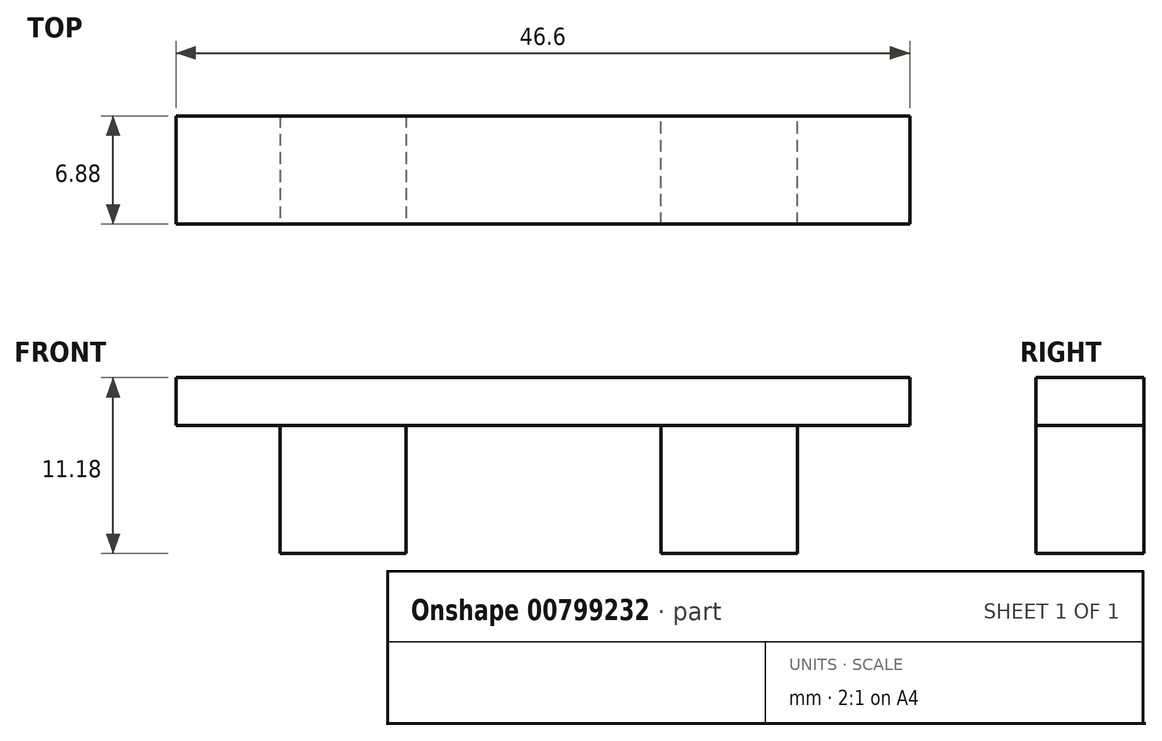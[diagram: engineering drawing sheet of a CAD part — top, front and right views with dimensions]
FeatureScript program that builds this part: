
annotation { "Feature Type Name" : "Feature", "Feature Type Description" : "" }
export const myFeature = defineFeature(function(context is Context, id is Id, definition is map)
    precondition{}
    {
        {
            var Q0;
            Q0=qCreatedBy(makeId("Top.planeOp"),FACE);
            var sketch = newSketch(context, id + "F0", { "sketchPlane" : qUnion([Q0])});
            skLineSegment(sketch, "E0.bottom", {"start": v(0, 0) * mm, "end": v(8.01, 0) * mm});
            skLineSegment(sketch, "E0.top", {"start": v(0, -6.88) * mm, "end": v(8.01, -6.88) * mm});
            skLineSegment(sketch, "E0.left", {"start": v(0, 0) * mm, "end": v(0, -6.88) * mm});
            skLineSegment(sketch, "E0.right", {"start": v(8.01, 0) * mm, "end": v(8.01, -6.88) * mm});
            skLineSegment(sketch, "E1.bottom", {"start": v(24.2, -6.88) * mm, "end": v(32.86, -6.88) * mm});
            skLineSegment(sketch, "E1.top", {"start": v(24.2, 0) * mm, "end": v(32.86, 0) * mm});
            skLineSegment(sketch, "E1.left", {"start": v(24.2, -6.88) * mm, "end": v(24.2, 0) * mm});
            skLineSegment(sketch, "E1.right", {"start": v(32.86, -6.88) * mm, "end": v(32.86, 0) * mm});
            skSolve(sketch);
        }
        {
            var Q0;
            Q0=makeQuery(id+"F0.imprint","IMPRINT",FACE,{"disambiguationData":[TD([[makeQuery(id+"F0.imprint","IMPRINT",EDGE,{"derivedFrom":sQuery(id+"F0.wireOp",EDGE,"E0.bottom")}),-1.0]])]});
            var Q1;
            Q1=makeQuery(id+"F0.imprint","IMPRINT",FACE,{"disambiguationData":[TD([[makeQuery(id+"F0.imprint","IMPRINT",EDGE,{"derivedFrom":sQuery(id+"F0.wireOp",EDGE,"E1.bottom")}),1.0]])]});
            extrude(context, id + "F1", {"entities" : qUnion([Q0, Q1]), "depth" : 8.13 * mm, "offsetDistance" : 25.4 * mm});
        }
        {
            var Q0;
            Q0=makeQuery(id+"F1.opExtrude","CAP_FACE",FACE,{"disambiguationData":[OSD([sQuery(id+"F0.wireOp",EDGE,"E0.bottom"),sQuery(id+"F0.wireOp",EDGE,"E0.top"),sQuery(id+"F0.wireOp",EDGE,"E0.left"),sQuery(id+"F0.wireOp",EDGE,"E0.right")])],"isStart":false});
            var sketch = newSketch(context, id + "F2", { "sketchPlane" : qUnion([Q0])});
            skLineSegment(sketch, "E2.bottom", {"start": v(-6.6, 0) * mm, "end": v(40, 0) * mm});
            skLineSegment(sketch, "E2.top", {"start": v(-6.6, -6.88) * mm, "end": v(40, -6.88) * mm});
            skLineSegment(sketch, "E2.left", {"start": v(-6.6, 0) * mm, "end": v(-6.6, -6.88) * mm});
            skLineSegment(sketch, "E2.right", {"start": v(40, 0) * mm, "end": v(40, -6.88) * mm});
            skSolve(sketch);
        }
        {
            var Q0;
            {var subQ2=sQuery(id+"F2.wireOp",EDGE,"E2.left");Q0=makeQuery(id+"F2.imprint","IMPRINT",FACE,{"disambiguationData":[TD([[makeQuery(id+"F2.imprint","IMPRINT",EDGE,{"derivedFrom":subQ2}),1.0]])]});}
            var Q1;
            {var subQ2=sQuery(id+"F2.wireOp",EDGE,"E2.right");Q1=makeQuery(id+"F2.imprint","IMPRINT",FACE,{"disambiguationData":[TD([[makeQuery(id+"F2.imprint","IMPRINT",EDGE,{"derivedFrom":subQ2}),-1.0]])]});}
            var Q2;
            {var subQ1=makeQuery(id+"F1.opExtrude","CAP_EDGE",EDGE,{"disambiguationData":[OSD([sQuery(id+"F0.wireOp",EDGE,"E0.left")])],"isStart":false});Q2=makeQuery(id+"F2.imprint","IMPRINT",FACE,{"disambiguationData":[TD([[makeQuery(id+"F2.imprint","IMPRINT",EDGE,{"derivedFrom":subQ1}),1.0]])]});}
            extrude(context, id + "F3", {"entities" : qUnion([Q0, Q1, Q2]), "depth" : 3.05 * mm, "offsetDistance" : 25.4 * mm});
        }
    });
